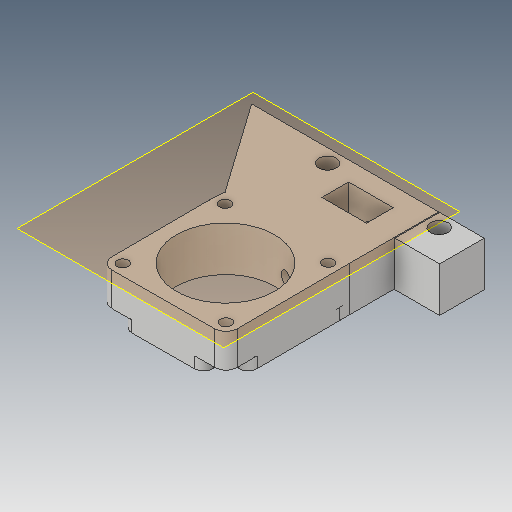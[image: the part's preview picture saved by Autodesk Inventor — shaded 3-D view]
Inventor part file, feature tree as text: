
AUTODESK INVENTOR PART (.ipt)
format: ipt  version: 2019.4 (Build 234330000, 330)  size: 222,208 bytes
history: native  units: mm
features: sketch x6, extrude x5, reference x3, projected_geometry x3, other x3, plane x2, chamfer x1, hole x1, fillet x1
ambient origin geometry x8: Origin, YZ Plane, XZ Plane, XY Plane, X Axis, Y Axis, Z Axis, Center Point
bodies: Solid1 (feature_tree)
feature tree (25):
  plane  "Work Plane1"
  sketch  "Sketch1"  dims[d0=10.0mm d1=0.0mm d2=10.0mm d3=0.0mm]
  plane  "Work Plane2"
  extrude  "Extrusion1"  Depth=10.0mm TaperAngle=0.0deg
  extrude  "Extrusion2"  Depth=10.0mm
  chamfer  "Chamfer1"  Distance=10.0mm Angle=45.0deg
  extrude  "Extrusion3"  Depth=30.0mm TaperAngle=0.0deg
  extrude  "Extrusion4"  Depth=10.0mm
  hole  "Hole1"  [1 undecoded]
  fillet  "Fillet1"  Radius=2.0mm
  extrude  "Extrusion5"  Depth=2.0mm TaperAngle=0.0deg
  reference  "Reference1"
  sketch  "Sketch2"  dims[d4=10.0mm d5=10.0mm d6=10.0mm d7=2.0mm d8=45.0deg]
  reference  "Reference2"
  projected_geometry  "Projected Loop1"
  sketch  "Sketch3"  dims[d9=2.9mm d10=30.0mm d11=0.0mm]
  projected_geometry  "Projected Loop2"
  sketch  "Sketch4"  dims[d12=10.0mm d13=6.0mm]
  sketch  "Sketch5"  dims[d14=1.45mm d15=30.0mm d16=0.0mm]
  projected_geometry  "Projected Loop3"
  sketch  "Sketch6"  dims[d17=2.5mm d18=6.0mm d19=5.0mm d20=2.5mm d21=90.0deg d22=8.0mm d23=20.594885mm d24=2.0mm d25=30.0mm d26=0.0mm]
  reference  "Reference3"
  other  "<userpath>\Dropbox\cellSTORM\cellSTORM_v6.iam"
  other  "cellSTORM_v6.iam"
  other  "cellSTORM_v5_cellphonestage:1"
note: 1 required parameter value undecoded (feature->parameter linkage not recoverable at this tier; creation-order binding heuristic only, values carry confidence <= 0.55)
